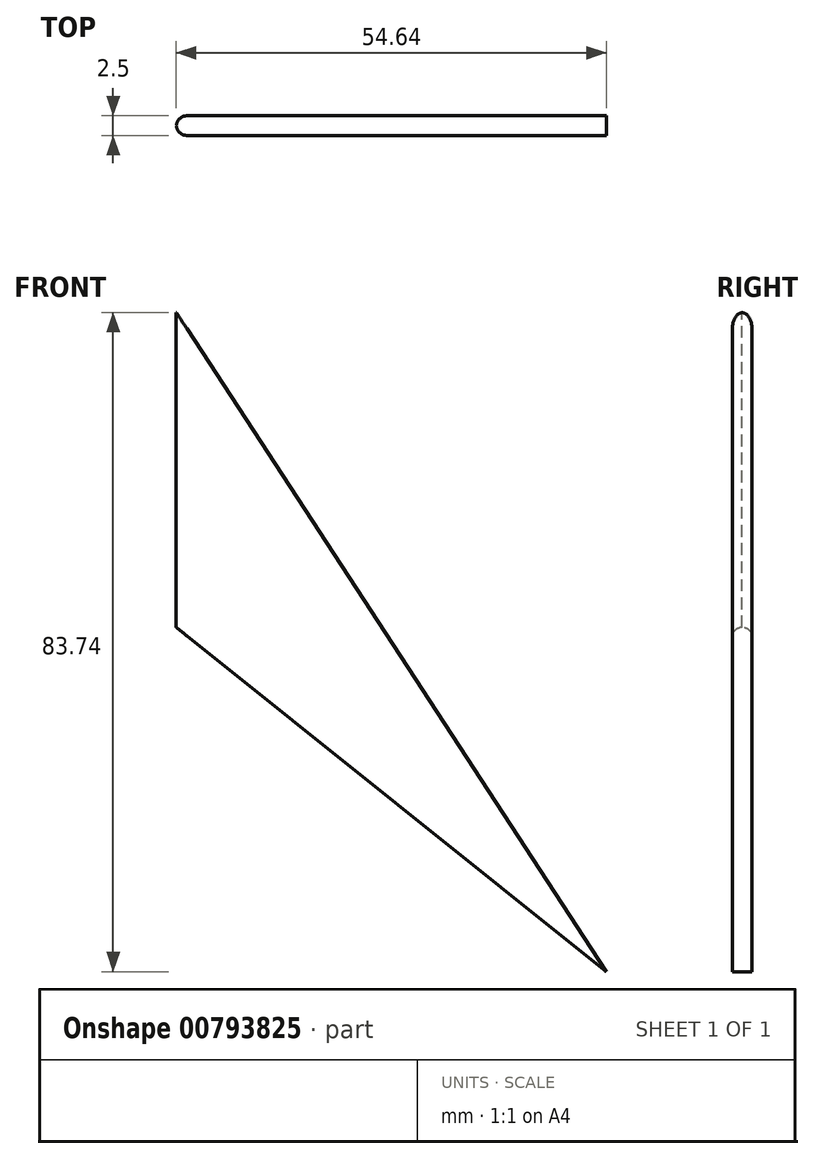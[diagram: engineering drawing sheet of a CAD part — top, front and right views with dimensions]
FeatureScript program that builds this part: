
annotation { "Feature Type Name" : "Feature", "Feature Type Description" : "" }
export const myFeature = defineFeature(function(context is Context, id is Id, definition is map)
    precondition{}
    {
        {
            var Q0;
            Q0=qCreatedBy(makeId("Front.planeOp"),FACE);
            var sketch = newSketch(context, id + "F0", { "sketchPlane" : qUnion([Q0])});
            skLineSegment(sketch, "E0", {"start": v(0, 0) * mm, "end": v(0, 40) * mm});
            skLineSegment(sketch, "E1", {"start": v(0, 40) * mm, "end": v(54.64, -43.75) * mm});
            skLineSegment(sketch, "E2", {"start": v(0, 0) * mm, "end": v(54.64, -43.75) * mm});
            skSolve(sketch);
        }
        {
            var Q0;
            Q0 = qSketchRegion(id + "F0", true);
            extrude(context, id + "F1", {"entities" : qUnion([Q0]), "depth" : 2.5 * mm, "offsetDistance" : 25.4 * mm});
        }
        {
            var Q0;
            Q0=makeQuery(id+"F1.opExtrude","CAP_EDGE",EDGE,{"disambiguationData":[OSD([sQuery(id+"F0.wireOp",EDGE,"E0")])],"isStart":false});
            var Q1;
            Q1=makeQuery(id+"F1.opExtrude","CAP_EDGE",EDGE,{"disambiguationData":[OSD([sQuery(id+"F0.wireOp",EDGE,"E0")])],"isStart":true});
            fillet(context, id + "F2", {"entities" : qUnion([Q0, Q1]), "radius" : 1.35 * mm, "tangentPropagation" : true, "allowEdgeOverflow" : false});
        }
    });
